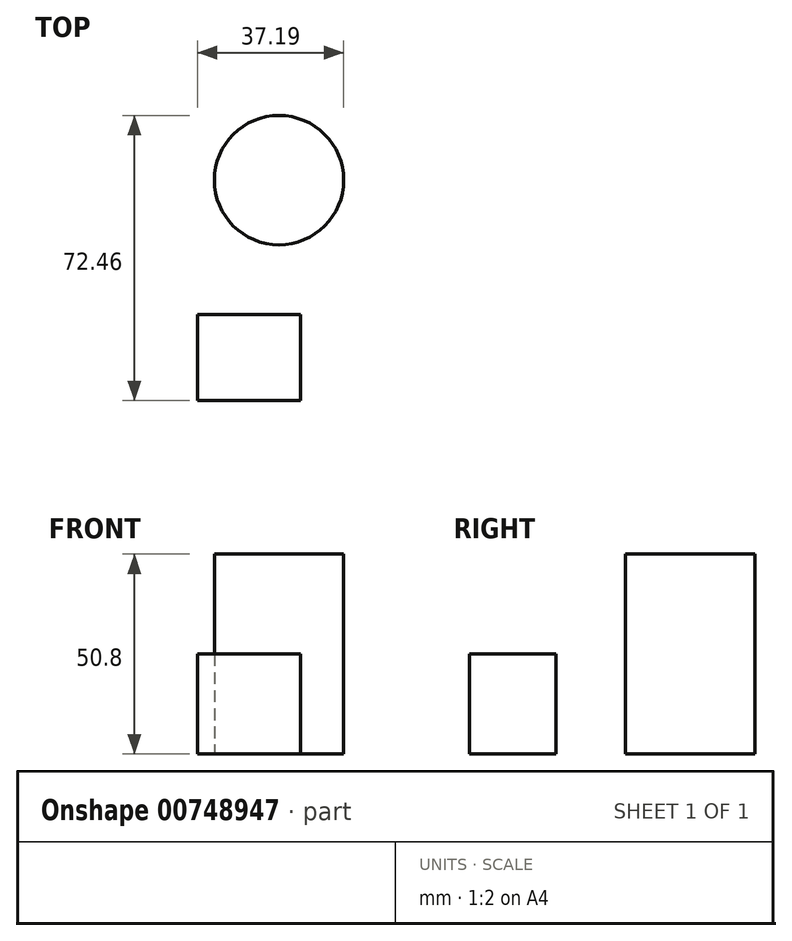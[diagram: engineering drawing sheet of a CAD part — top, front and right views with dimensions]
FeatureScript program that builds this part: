
annotation { "Feature Type Name" : "Feature", "Feature Type Description" : "" }
export const myFeature = defineFeature(function(context is Context, id is Id, definition is map)
    precondition{}
    {
        {
            var Q0;
            Q0=qCreatedBy(makeId("Top.planeOp"),FACE);
            var sketch = newSketch(context, id + "F0", { "sketchPlane" : qUnion([Q0])});
            skLineSegment(sketch, "E0.bottom", {"start": v(0, 0) * mm, "end": v(26.26, 0) * mm});
            skLineSegment(sketch, "E0.top", {"start": v(0, -21.92) * mm, "end": v(26.26, -21.92) * mm});
            skLineSegment(sketch, "E0.left", {"start": v(0, 0) * mm, "end": v(0, -21.92) * mm});
            skLineSegment(sketch, "E0.right", {"start": v(26.26, 0) * mm, "end": v(26.26, -21.92) * mm});
            skCircle(sketch, "E1", {"center": v(20.75, 34.1) * mm, "radius": 16.43 * mm});
            skSolve(sketch);
        }
        {
            var Q0;
            Q0=makeQuery(id+"F0.imprint","IMPRINT",FACE,{"disambiguationData":[TD([[makeQuery(id+"F0.imprint","IMPRINT",EDGE,{"derivedFrom":sQuery(id+"F0.wireOp",EDGE,"E0.bottom")}),-1.0]])]});
            extrude(context, id + "F1", {"entities" : qUnion([Q0]), "depth" : 25.4 * mm, "offsetDistance" : 25.4 * mm});
        }
        {
            var Q0;
            Q0=makeQuery(id+"F0.imprint","IMPRINT",FACE,{"disambiguationData":[TD([[makeQuery(id+"F0.imprint","IMPRINT",EDGE,{"derivedFrom":sQuery(id+"F0.wireOp",EDGE,"E1")}),1.0]])]});
            extrude(context, id + "F2", {"entities" : qUnion([Q0]), "depth" : 50.8 * mm, "offsetDistance" : 25.4 * mm});
        }
    });
